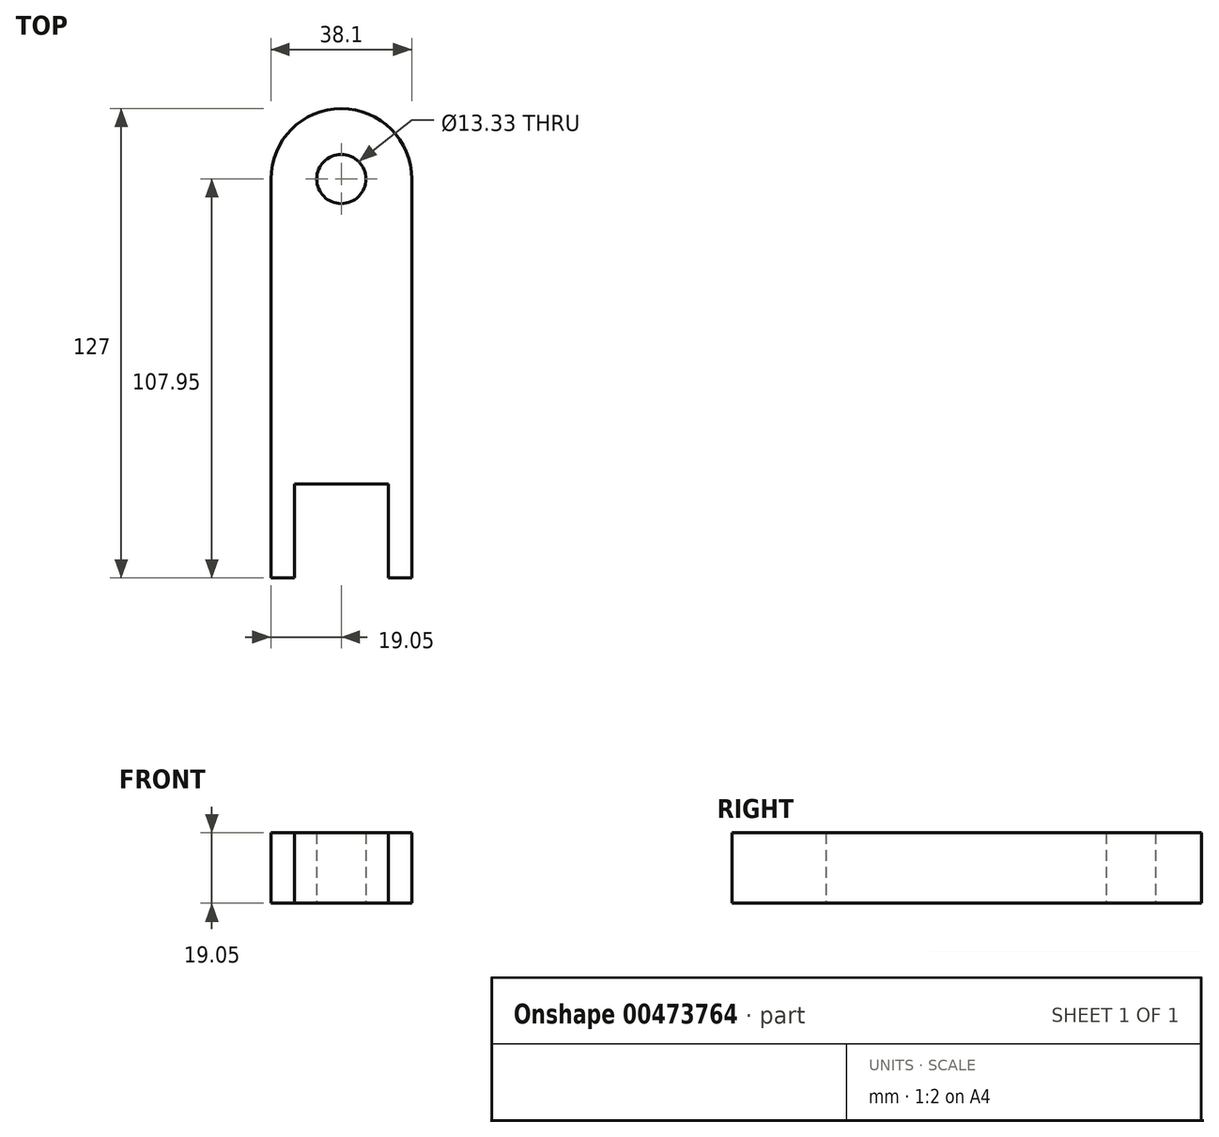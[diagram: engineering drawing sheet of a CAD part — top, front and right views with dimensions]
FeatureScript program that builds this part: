
annotation { "Feature Type Name" : "Feature", "Feature Type Description" : "" }
export const myFeature = defineFeature(function(context is Context, id is Id, definition is map)
    precondition{}
    {
        {
            var Q0;
            Q0=qCreatedBy(makeId("Top.planeOp"),FACE);
            var sketch = newSketch(context, id + "F0", { "sketchPlane" : qUnion([Q0])});
            skCircle(sketch, "E0", {"center": v(0, 0) * mm, "radius": 19.05 * mm});
            skLineSegment(sketch, "E1.bottom", {"start": v(19.05, 0) * mm, "end": v(-19.05, 0) * mm});
            skLineSegment(sketch, "E1.top", {"start": v(19.05, -82.55) * mm, "end": v(-19.05, -82.55) * mm});
            skLineSegment(sketch, "E1.left", {"start": v(19.05, 0) * mm, "end": v(19.05, -82.55) * mm});
            skLineSegment(sketch, "E1.right", {"start": v(-19.05, 0) * mm, "end": v(-19.05, -82.55) * mm});
            skLineSegment(sketch, "E2.bottom", {"start": v(-19.05, -82.55) * mm, "end": v(-12.7, -82.55) * mm});
            skLineSegment(sketch, "E2.top", {"start": v(-19.05, -107.95) * mm, "end": v(-12.7, -107.95) * mm});
            skLineSegment(sketch, "E2.left", {"start": v(-19.05, -82.55) * mm, "end": v(-19.05, -107.95) * mm});
            skLineSegment(sketch, "E2.right", {"start": v(-12.7, -82.55) * mm, "end": v(-12.7, -107.95) * mm});
            skLineSegment(sketch, "E3.bottom", {"start": v(19.05, -82.55) * mm, "end": v(12.7, -82.55) * mm});
            skLineSegment(sketch, "E3.top", {"start": v(19.05, -107.95) * mm, "end": v(12.7, -107.95) * mm});
            skLineSegment(sketch, "E3.left", {"start": v(19.05, -82.55) * mm, "end": v(19.05, -107.95) * mm});
            skLineSegment(sketch, "E3.right", {"start": v(12.7, -82.55) * mm, "end": v(12.7, -107.95) * mm});
            skCircle(sketch, "E4", {"center": v(0, 0) * mm, "radius": 6.67 * mm});
            skSolve(sketch);
        }
        {
            var Q0;
            Q0 = qSketchRegion(id + "F0", true);
            extrude(context, id + "F1", {"entities" : qUnion([Q0]), "depth" : 19.05 * mm});
        }
    });
